# Revit family: Sabiana Polaris
name_source: partatom
category: Attrezzatura meccanica
revit_build: Autodesk Revit 2017 (Build: 20181011_1645(x64)
units: mm (PartAtom-declared; Revit-internal decimal feet)

## family parameters
Basato su piano di lavoro = Sì
Condiviso = No
Numero OmniClass = 23.75.00.00
Punto di calcolo locali = No
Quota connettore circolare = Usa diametro
Sempre verticale = Sì
Taglio con vuoti quando caricato = No
Tipo di parte = Normale
Titolo OmniClass = Climate Control (HVAC)

## types (9) — shared parameters
Data = PolarisData
Lamiera = lamiera
Modello = Polaris
Produttore = Sabiana
Prospetto di default = 1219 mm
Scarico = 15 mm  [stored 0.0492126 ft]
URL = https://www.sabiana.it
batteria = lamelle
ganci = Ferro
lancio = trasp
tubi = Ferro

## per-type parameters (varying)
| type | gr |
| gr 0 | 0 |
| gr 1 | 1 |
| gr 3 | 3 |
| gr 4 | 4 |
| gr 5 | 5 |
| gr 6 | 6 |
| gr 7 | 7 |
| gr 8 | 8 |
| gr 9 | 9 |

note: [stored X ft] marks values corroborated as IEEE doubles in the binary element streams (Revit-internal decimal feet)
